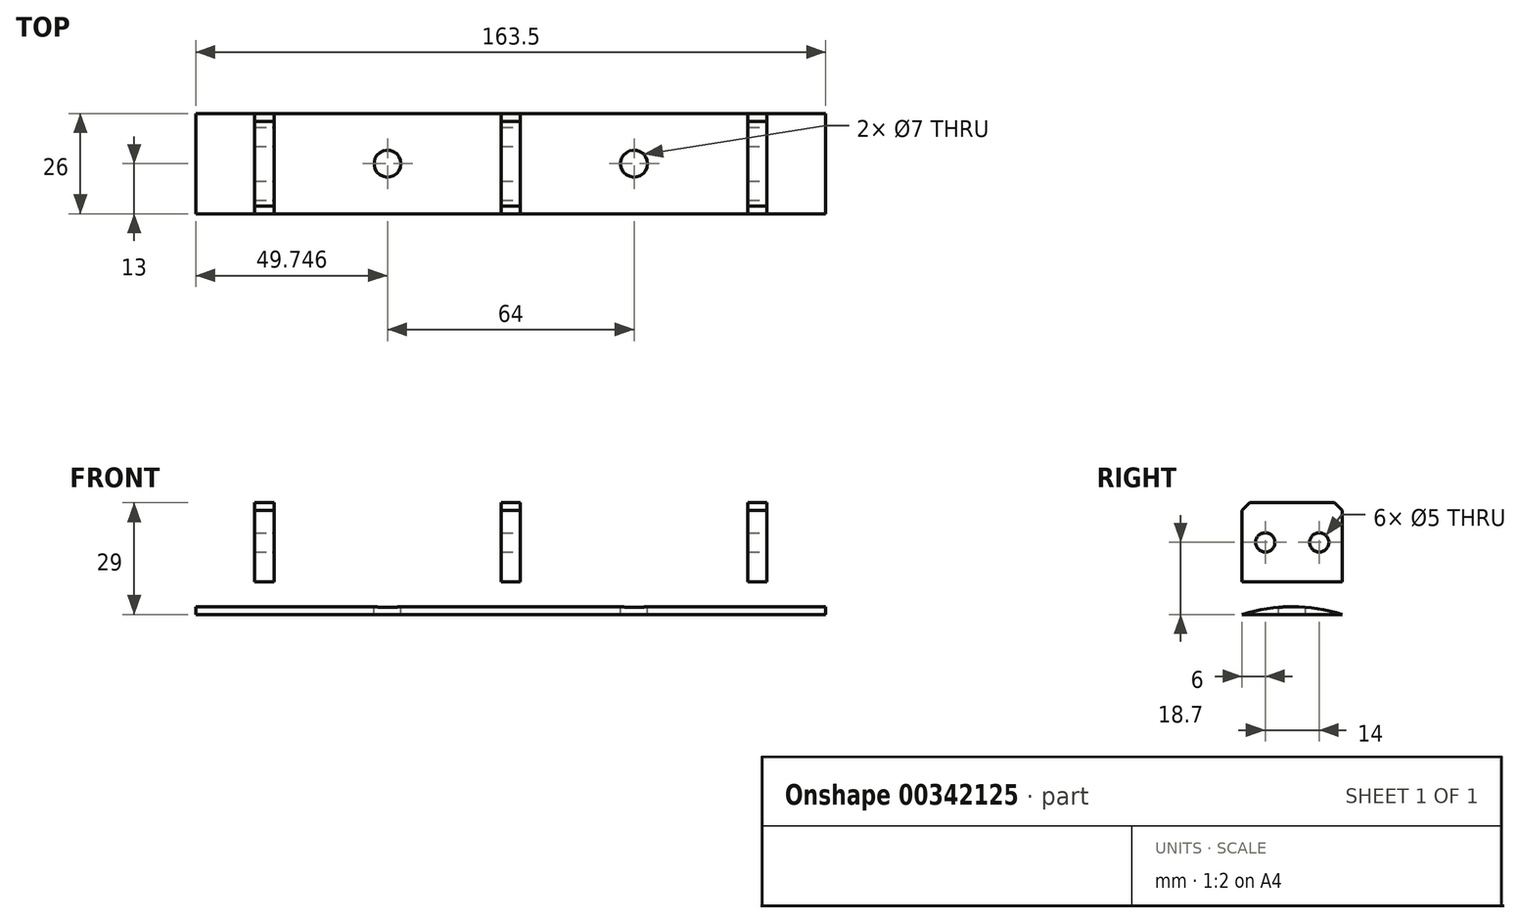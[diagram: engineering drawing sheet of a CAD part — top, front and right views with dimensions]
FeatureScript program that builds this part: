
annotation { "Feature Type Name" : "Feature", "Feature Type Description" : "" }
export const myFeature = defineFeature(function(context is Context, id is Id, definition is map)
    precondition{}
    {
        {
            var Q0;
            Q0=qCreatedBy(makeId("Front.planeOp"),FACE);
            var sketch = newSketch(context, id + "F0", { "sketchPlane" : qUnion([Q0])});
            skLineSegment(sketch, "E0.bottom", {"start": v(-71.23, 0) * mm, "end": v(92.27, 0) * mm});
            skLineSegment(sketch, "E0.top", {"start": v(-71.23, 8.5) * mm, "end": v(-55.98, 8.5) * mm});
            skLineSegment(sketch, "E0.left", {"start": v(-71.23, 0) * mm, "end": v(-71.23, 8.5) * mm});
            skLineSegment(sketch, "E0.right", {"start": v(92.27, 0) * mm, "end": v(92.27, 8.5) * mm});
            skLineSegment(sketch, "E1.top", {"start": v(-55.98, 29) * mm, "end": v(-50.98, 29) * mm});
            skLineSegment(sketch, "E1.left", {"start": v(-55.98, 8.5) * mm, "end": v(-55.98, 29) * mm});
            skLineSegment(sketch, "E1.right", {"start": v(-50.98, 8.5) * mm, "end": v(-50.98, 29) * mm});
            skLineSegment(sketch, "E2.top", {"start": v(8.02, 29) * mm, "end": v(13.02, 29) * mm});
            skLineSegment(sketch, "E2.left", {"start": v(8.02, 8.5) * mm, "end": v(8.02, 29) * mm});
            skLineSegment(sketch, "E2.right", {"start": v(13.02, 8.5) * mm, "end": v(13.02, 29) * mm});
            skLineSegment(sketch, "E3.top", {"start": v(72.02, 29) * mm, "end": v(77.02, 29) * mm});
            skLineSegment(sketch, "E3.left", {"start": v(72.02, 8.5) * mm, "end": v(72.02, 29) * mm});
            skLineSegment(sketch, "E3.right", {"start": v(77.02, 8.5) * mm, "end": v(77.02, 29) * mm});
            skLineSegment(sketch, "E4.trimOffspring", {"start": v(-50.98, 8.5) * mm, "end": v(8.02, 8.5) * mm});
            skLineSegment(sketch, "E5.trimOffspring", {"start": v(13.02, 8.5) * mm, "end": v(72.02, 8.5) * mm});
            skLineSegment(sketch, "E6.trimOffspring", {"start": v(77.02, 8.5) * mm, "end": v(92.27, 8.5) * mm});
            skSolve(sketch);
        }
        {
            var Q0;
            Q0=makeQuery(id+"F0.imprint","IMPRINT",FACE,{"disambiguationData":[TD([[makeQuery(id+"F0.imprint","IMPRINT",EDGE,{"derivedFrom":sQuery(id+"F0.wireOp",EDGE,"E0.bottom")}),1.0]])]});
            var Q1;
            Q1=makeQuery(id+"F0.imprint","IMPRINT",FACE,{"disambiguationData":[TD([[makeQuery(id+"F0.imprint","IMPRINT",EDGE,{"derivedFrom":sQuery(id+"F0.wireOp",EDGE,"E3.top")}),-1.0]])]});
            extrude(context, id + "F1", {"entities" : qUnion([Q0, Q1]), "depth" : 26 * mm});
        }
        {
            var Q0;
            Q0=makeQuery(id+"F1.opExtrude","SWEPT_FACE",FACE,{"disambiguationData":[OSD([sQuery(id+"F0.wireOp",EDGE,"E0.right")])]});
            var sketch = newSketch(context, id + "F2", { "sketchPlane" : qUnion([Q0])});
            skLineSegment(sketch, "E7.0", {"start": v(-26, 8.5) * mm, "end": v(-26, 29) * mm});
            skLineSegment(sketch, "E8.0", {"start": v(0, 8.5) * mm, "end": v(0, 29) * mm});
            skLineSegment(sketch, "E9.0.1", {"start": v(0, 29) * mm, "end": v(-26, 29) * mm});
            skLineSegment(sketch, "E9.0.2", {"start": v(-26, 29) * mm, "end": v(-26, 8.5) * mm});
            skLineSegment(sketch, "E9.0.3", {"start": v(-26, 8.5) * mm, "end": v(0, 8.5) * mm});
            skLineSegment(sketch, "E10.0.0", {"start": v(0, 0) * mm, "end": v(0, 8.5) * mm});
            skLineSegment(sketch, "E10.0.1", {"start": v(0, 8.5) * mm, "end": v(-26, 8.5) * mm});
            skLineSegment(sketch, "E10.0.2", {"start": v(-26, 8.5) * mm, "end": v(-26, 0) * mm});
            skLineSegment(sketch, "E10.0.3", {"start": v(-26, 0) * mm, "end": v(-13, 0) * mm});
            skLineSegment(sketch, "E11", {"start": v(-13, 0) * mm, "end": v(-13, -49.65) * mm});
            skLineSegment(sketch, "E12", {"start": v(-26, 0) * mm, "end": v(-13, -41.51) * mm});
            skLineSegment(sketch, "E13", {"start": v(-13, -41.51) * mm, "end": v(0, 0) * mm});
            skArc(sketch, "E14", {"start": v(-26, 0) * mm, "mid": v(-13, 1.99) * mm, "end": v(0, 0) * mm});
            skLineSegment(sketch, "E15.0", {"start": v(-26, 0) * mm, "end": v(0, 0) * mm});
            skLineSegment(sketch, "E16", {"start": v(-13, 0) * mm, "end": v(-13, 18.7) * mm});
            skLineSegment(sketch, "E17", {"start": v(-13, 18.7) * mm, "end": v(-20, 18.7) * mm});
            skLineSegment(sketch, "E18", {"start": v(-13, 18.7) * mm, "end": v(-6, 18.7) * mm});
            skSolve(sketch);
        }
        {
            var Q0;
            {var subQ0=sQuery(id+"F2.wireOp",EDGE,"E14");Q0=makeQuery(id+"F2.imprint","IMPRINT",FACE,{"disambiguationData":[TD([[makeQuery(id+"F2.imprint","IMPRINT",EDGE,{"derivedFrom":subQ0}),-1.0]])]});}
            extrude(context, id + "F3", {"entities" : qUnion([Q0]), "operationType" : NewBodyOperationType.REMOVE, "oppositeDirection" : true, "depth" : 200 * mm});
        }
        {
            var Q0;
            Q0=makeQuery(id+"F1.opExtrude","CAP_EDGE",EDGE,{"disambiguationData":[OSD([sQuery(id+"F0.wireOp",EDGE,"E3.top")])],"isStart":true});
            var Q1;
            Q1=makeQuery(id+"F1.opExtrude","CAP_EDGE",EDGE,{"disambiguationData":[OSD([sQuery(id+"F0.wireOp",EDGE,"E3.top")])],"isStart":false});
            var Q2;
            Q2=makeQuery(id+"F1.opExtrude","CAP_EDGE",EDGE,{"disambiguationData":[OSD([sQuery(id+"F0.wireOp",EDGE,"E2.top")])],"isStart":false});
            var Q3;
            Q3=makeQuery(id+"F1.opExtrude","CAP_EDGE",EDGE,{"disambiguationData":[OSD([sQuery(id+"F0.wireOp",EDGE,"E2.top")])],"isStart":true});
            var Q4;
            Q4=makeQuery(id+"F1.opExtrude","CAP_EDGE",EDGE,{"disambiguationData":[OSD([sQuery(id+"F0.wireOp",EDGE,"E1.top")])],"isStart":false});
            var Q5;
            Q5=makeQuery(id+"F1.opExtrude","CAP_EDGE",EDGE,{"disambiguationData":[OSD([sQuery(id+"F0.wireOp",EDGE,"E1.top")])],"isStart":true});
            chamfer(context, id + "F4", {"entities" : qUnion([Q0, Q1, Q2, Q3, Q4, Q5]), "chamferType" : ChamferType.OFFSET_ANGLE, "width" : 2 * mm, "oppositeDirection" : false, "angle" : 45 * degree, "tangentPropagation" : true});
        }
        {
            var Q0;
            Q0=sQuery(id+"F2.wireOp",VERTEX,"E17.end");
            var Q1;
            Q1=sQuery(id+"F2.wireOp",VERTEX,"E18.end");
            var Q2;
            Q2=makeQuery(id+"F1.opExtrude","SWEPT_BODY",BODY,{"disambiguationData":[OSD([sQuery(id+"F0.wireOp",EDGE,"E0.bottom"),sQuery(id+"F0.wireOp",EDGE,"E0.top"),sQuery(id+"F0.wireOp",EDGE,"E0.left"),sQuery(id+"F0.wireOp",EDGE,"E0.right"),sQuery(id+"F0.wireOp",EDGE,"E1.top"),sQuery(id+"F0.wireOp",EDGE,"E1.left"),sQuery(id+"F0.wireOp",EDGE,"E1.right"),sQuery(id+"F0.wireOp",EDGE,"E2.top"),sQuery(id+"F0.wireOp",EDGE,"E2.left"),sQuery(id+"F0.wireOp",EDGE,"E2.right"),sQuery(id+"F0.wireOp",EDGE,"E3.top"),sQuery(id+"F0.wireOp",EDGE,"E3.left"),sQuery(id+"F0.wireOp",EDGE,"E3.right"),sQuery(id+"F0.wireOp",EDGE,"E4.trimOffspring"),sQuery(id+"F0.wireOp",EDGE,"E5.trimOffspring"),sQuery(id+"F0.wireOp",EDGE,"E6.trimOffspring")])]});
            hole(context, id + "F5", {"style" : HoleStyle.SIMPLE, "endStyle" : HoleEndStyle.BLIND, "holeDiameter" : 5 * mm, "holeDepth" : 300 * mm, "tappedDepth" : 12 * mm, "tapClearance" : 3, "locations" : qUnion([Q0, Q1]), "scope" : qUnion([Q2])});
        }
        {
            var Q0;
            Q0=makeQuery(id+"F1.opExtrude","CAP_VERTEX",VERTEX,{"disambiguationData":[OSD([sQuery(id+"F0.wireOp",EDGE,"E2.right"),sQuery(id+"F0.wireOp",EDGE,"E5.trimOffspring")])],"isStart":false});
            var Q1;
            Q1=makeQuery(id+"F1.opExtrude","CAP_VERTEX",VERTEX,{"disambiguationData":[OSD([sQuery(id+"F0.wireOp",EDGE,"E2.right"),sQuery(id+"F0.wireOp",EDGE,"E5.trimOffspring")])],"isStart":true});
            var Q2;
            Q2=makeQuery(id+"F1.opExtrude","CAP_VERTEX",VERTEX,{"disambiguationData":[OSD([sQuery(id+"F0.wireOp",EDGE,"E2.left"),sQuery(id+"F0.wireOp",EDGE,"E4.trimOffspring")])],"isStart":false});
            cPlane(context, id + "F6", {"entities" : qUnion([Q0, Q1, Q2]), "cplaneType" : CPlaneType.THREE_POINT, "offset" : 25 * mm, "width" : 150 * mm, "height" : 150 * mm});
        }
        {
            var Q0;
            Q0=qCreatedBy(id+"F6.planeOp",FACE);
            var sketch = newSketch(context, id + "F7", { "sketchPlane" : qUnion([Q0])});
            skPoint(sketch, "E19.0", {"position": v(10.52, 26) * mm});
            skLineSegment(sketch, "E20", {"start": v(10.52, 26) * mm, "end": v(10.52, 13) * mm});
            skLineSegment(sketch, "E21", {"start": v(10.52, 13) * mm, "end": v(42.52, 13) * mm});
            skLineSegment(sketch, "E22", {"start": v(10.52, 13) * mm, "end": v(-21.48, 13) * mm});
            skSolve(sketch);
        }
        {
            var Q0;
            Q0=sQuery(id+"F7.wireOp",VERTEX,"E22.end");
            var Q1;
            Q1=sQuery(id+"F7.wireOp",VERTEX,"E21.end");
            var Q2;
            Q2=makeQuery(id+"F1.opExtrude","SWEPT_BODY",BODY,{"disambiguationData":[OSD([sQuery(id+"F0.wireOp",EDGE,"E0.bottom"),sQuery(id+"F0.wireOp",EDGE,"E0.top"),sQuery(id+"F0.wireOp",EDGE,"E0.left"),sQuery(id+"F0.wireOp",EDGE,"E0.right"),sQuery(id+"F0.wireOp",EDGE,"E1.top"),sQuery(id+"F0.wireOp",EDGE,"E1.left"),sQuery(id+"F0.wireOp",EDGE,"E1.right"),sQuery(id+"F0.wireOp",EDGE,"E2.top"),sQuery(id+"F0.wireOp",EDGE,"E2.left"),sQuery(id+"F0.wireOp",EDGE,"E2.right"),sQuery(id+"F0.wireOp",EDGE,"E3.top"),sQuery(id+"F0.wireOp",EDGE,"E3.left"),sQuery(id+"F0.wireOp",EDGE,"E3.right"),sQuery(id+"F0.wireOp",EDGE,"E4.trimOffspring"),sQuery(id+"F0.wireOp",EDGE,"E5.trimOffspring"),sQuery(id+"F0.wireOp",EDGE,"E6.trimOffspring")])]});
            hole(context, id + "F8", {"style" : HoleStyle.SIMPLE, "endStyle" : HoleEndStyle.BLIND, "oppositeDirection" : true, "holeDiameter" : 7 * mm, "holeDepth" : 300 * mm, "tappedDepth" : 12 * mm, "tapClearance" : 3, "locations" : qUnion([Q0, Q1]), "scope" : qUnion([Q2])});
        }
    });
